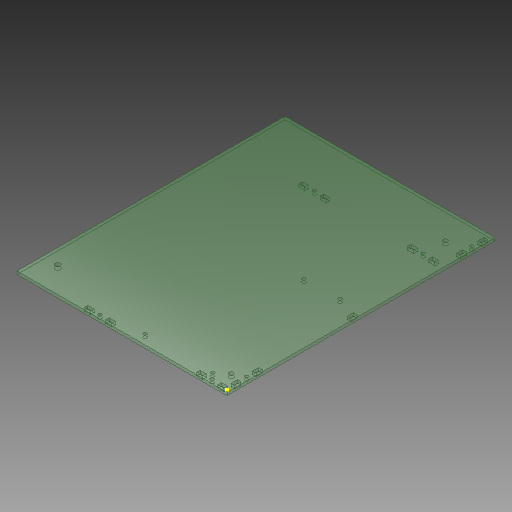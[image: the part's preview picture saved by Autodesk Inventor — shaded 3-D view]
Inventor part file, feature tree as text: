
AUTODESK INVENTOR PART (.ipt)
format: ipt  version: 2017 (Build 210142000, 142)  size: 811,520 bytes
history: native  units: mm
features: sketch x5, hole x3, projected_geometry x2, extrude x1
ambient origin geometry x8: Origin, YZ Plane, XZ Plane, XY Plane, X Axis, Y Axis, Z Axis, Center Point
bodies: Solid1 (feature_tree)
feature tree (11):
  extrude  "Extrusion1"  [1 undecoded]
  hole  "Hole2"  [1 undecoded]
  sketch  "Sketch3"  dims[d22=4.5mm d23=6.0mm d24=4.0mm d25=2.0mm d26=90.0deg d27=8.0mm d28=20.594885mm]
  hole  "Hole3"  [1 undecoded]
  hole  "Hole4"  [1 undecoded]
  sketch  "Sketch1"  dims[d0=3.0mm d1=0.0mm]
  sketch  "Sketch2"  dims[d15=3.4mm d16=6.0mm d17=4.0mm d18=2.0mm d19=90.0deg d20=8.0mm d21=20.594885mm]
  projected_geometry  "Projected Loop1"
  sketch  "Sketch4"  dims[d29=5.2mm d30=6.0mm d31=4.0mm d32=2.0mm d33=90.0deg d34=8.0mm d35=20.594885mm]
  projected_geometry  "Projected Loop2"
  sketch  "Sketch5"
note: 4 required parameter values undecoded (feature->parameter linkage not recoverable at this tier; creation-order binding heuristic only, values carry confidence <= 0.55)
